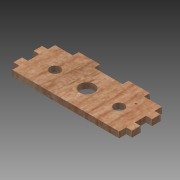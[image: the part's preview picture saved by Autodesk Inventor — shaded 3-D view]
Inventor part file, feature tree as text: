
AUTODESK INVENTOR PART (.ipt)
format: ipt  version: 2015 (Build 190159000, 159)  size: 280,064 bytes
history: native  units: mm
features: other x14, sketch x10, extrude x3, hole x2
ambient origin geometry x8: Origin, YZ Plane, XZ Plane, XY Plane, X Axis, Y Axis, Z Axis, Center Point
bodies: Body1 (feature_tree)
feature tree (29):
  other  "Blocks"
  extrude  "Extrusion2"  Depth=40.0mm
  hole  "Hole5"  [1 undecoded]
  sketch  "Sketch17"  dims[d53=9.6mm d54=6.0mm d55=4.0mm d56=2.0mm d57=90.0deg d58=4.0mm d59=0.0mm]
  hole  "Hole14"  [1 undecoded]
  extrude  "Extrusion4"  Depth=5.5mm
  extrude  "Extrusion5"  Depth=6.666667mm
  sketch  "Sketch46"  dims[d140=20.0mm]
  sketch  "Sketch47"  dims[d141=4.0mm d142=16.666667mm d143=20.0mm d144=5.5mm d145=5.5mm d146=0.0mm d29=1.0mm d30=1.0mm]
  sketch  "Sketch44"  dims[d138=5.5mm]
  sketch  "Sketch45"  dims[d139=0.0mm]
  sketch  "Sketch43"  dims[d134=8.0mm d135=6.666667mm]
  sketch  "Sketch10"  dims[d21=100.0mm d22=40.0mm]
  sketch  "Sketch16"  dims[d23=5.5mm d24=0.0mm d52=60.0mm]
  sketch  "Sketch34"  dims[d122=14.0mm d123=6.0mm d124=4.0mm d125=2.0mm d126=90.0deg d127=89.0mm d128=20.594885mm d131=20.0mm]
  sketch  "Sketch35"  dims[d132=5.5mm d133=5.5mm]
  other  "Block1"
  other  "Block2"
  other  "Block3"
  other  "Block4"
  other  "Block5"
  other  "Block6"
  other  "Block7"
  other  "Block5:1"
  other  "Block5:2"
  other  "Block6:1"
  other  "Block6:2"
  other  "Block7:1"
  other  "Block7:2"
note: 2 required parameter values undecoded (feature->parameter linkage not recoverable at this tier; creation-order binding heuristic only, values carry confidence <= 0.55)
